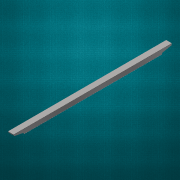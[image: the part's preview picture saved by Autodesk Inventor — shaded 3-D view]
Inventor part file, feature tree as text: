
AUTODESK INVENTOR PART (.ipt)
format: ipt  version: 2017 (Build 210142000, 142)  size: 240,640 bytes
history: native  units: in
note: dims shown in document units (in); Inventor stores cm internally (conversion verified against a paired STEP export)
features: sheet_metal_op x9, sketch x7, mirror x3, other x3, extrude x2
ambient origin geometry x8: Origin, YZ Plane, XZ Plane, XY Plane, X Axis, Y Axis, Z Axis, Center Point
bodies: Solid1 (feature_tree)
feature tree (24):
  sheet_metal_op  "Face1"
  sheet_metal_op  "Flange1"
  sheet_metal_op  "Hem1"
  sheet_metal_op  "Hem2"
  extrude  "Extrusion1"  Depth=3.0in
  mirror  "Mirror1"
  sheet_metal_op  "Flange2"
  extrude  "Extrusion2"  Depth=0.0625in
  mirror  "Mirror2"
  mirror  "Mirror3"
  sketch  "Sketch1"  dims[d0=80.75in d1=3.0in]
  other  "Plate1"
  sketch  "Sketch2"  dims[d2=0.0625in d3=0.0625in]
  other  "Plate2"
  sheet_metal_op  "Bend1"
  sheet_metal_op  "Corner1"
  sketch  "Sketch5"  dims[d6=0.0625in]
  sketch  "Sketch6"  dims[d7=2.5in d8=90.0deg d9=0.0625in]
  other  "Plate3"
  sheet_metal_op  "Bend2"
  sheet_metal_op  "Corner2"
  sketch  "Sketch7"  dims[d10=0.25in d11=0.0625in d12=0.0625in d13=0.0625in d14=0.0312in d15=0.125in d16=0.0625in d17=270.0deg d18=0.0625in d19=0.0625in d20=0.0625in d21=0.0312in d22=0.125in d23=0.0625in d24=270.0deg d25=0.0625in d26=0.0625in d27=0.75in d28=1.75in d29=5.0in d30=5.25in d31=1.0in d32=0.0in d33=0.0625in d34=0.0312in d35=0.125in d36=0.0625in d37=0.5in d38=90.0deg d39=0.0625in d40=0.25in d41=0.0625in d42=0.0625in d43=1.0in d44=0.0in]
  sketch  "Sketch3"  dims[d4=0.0312in]
  sketch  "Sketch4"  dims[d5=0.125in]
